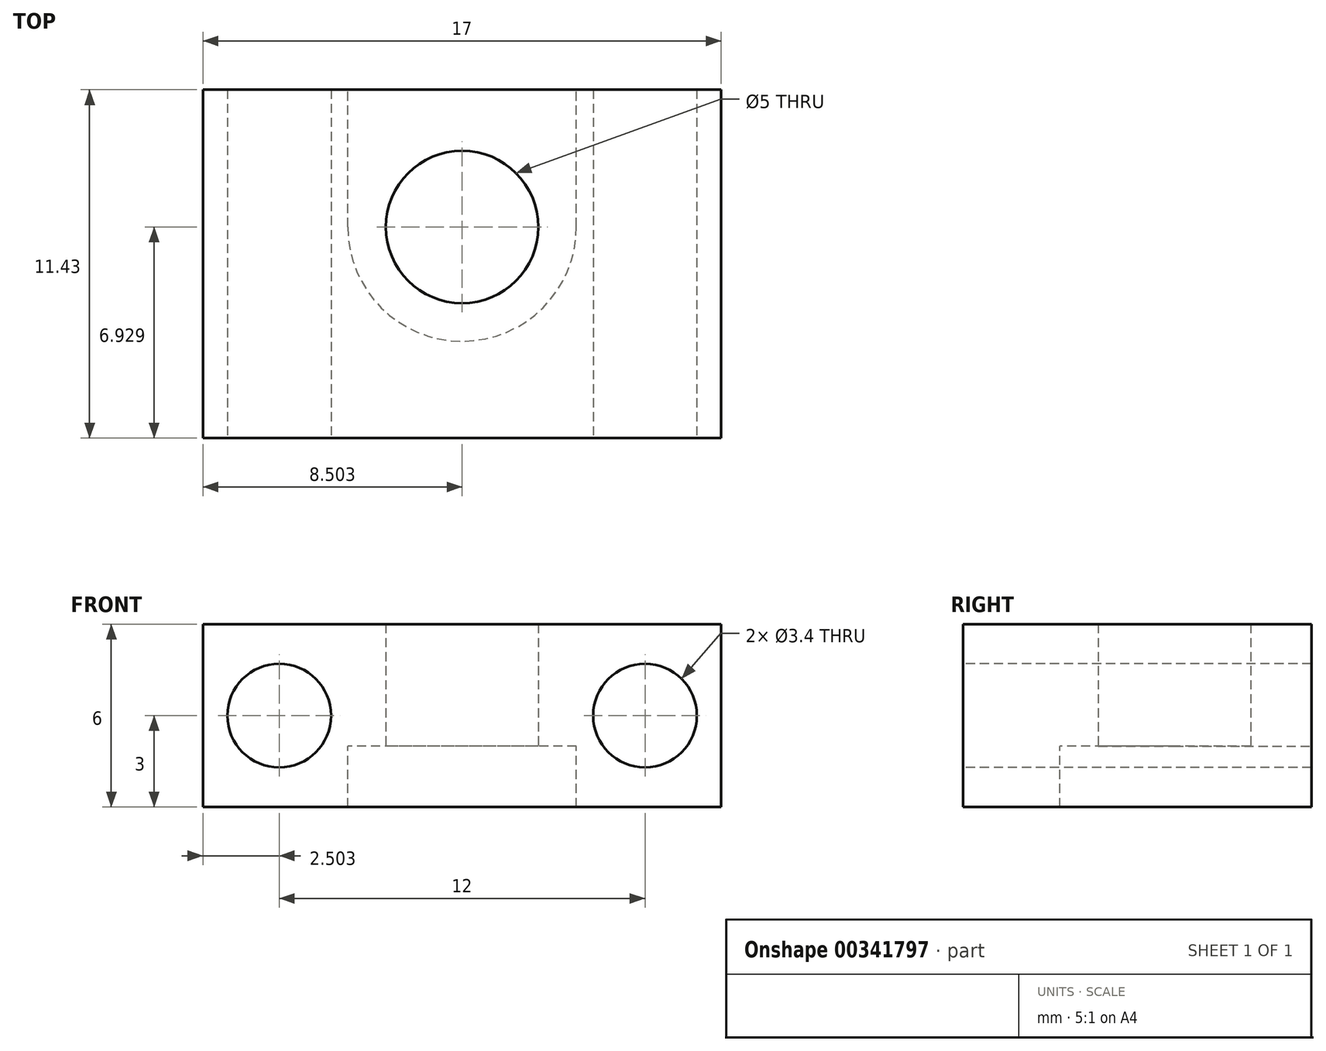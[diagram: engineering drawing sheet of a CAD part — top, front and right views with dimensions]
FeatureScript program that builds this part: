
annotation { "Feature Type Name" : "Feature", "Feature Type Description" : "" }
export const myFeature = defineFeature(function(context is Context, id is Id, definition is map)
    precondition{}
    {
        {
            var Q0;
            Q0=qCreatedBy(makeId("Top.planeOp"),FACE);
            var sketch = newSketch(context, id + "F0", { "sketchPlane" : qUnion([Q0])});
            skLineSegment(sketch, "E0.bottom", {"start": v(-26.33, 17.35) * mm, "end": v(-43.33, 17.35) * mm});
            skLineSegment(sketch, "E0.top", {"start": v(-26.33, 28.78) * mm, "end": v(-43.33, 28.78) * mm});
            skLineSegment(sketch, "E0.left", {"start": v(-26.33, 17.35) * mm, "end": v(-26.33, 28.78) * mm});
            skLineSegment(sketch, "E0.right", {"start": v(-43.33, 17.35) * mm, "end": v(-43.33, 28.78) * mm});
            skLineSegment(sketch, "E1", {"start": v(-34.83, 28.78) * mm, "end": v(-34.83, 17.35) * mm, "construction": true});
            skCircle(sketch, "E2", {"center": v(-34.83, 24.28) * mm, "radius": 2.5 * mm});
            skSolve(sketch);
        }
        {
            var Q0;
            Q0=makeQuery(id+"F0.imprint","IMPRINT",FACE,{"disambiguationData":[TD([[makeQuery(id+"F0.imprint","IMPRINT",EDGE,{"derivedFrom":sQuery(id+"F0.wireOp",EDGE,"E0.bottom")}),-1.0]])]});
            extrude(context, id + "F1", {"entities" : qUnion([Q0]), "depth" : 4 * mm});
        }
        {
            var Q0;
            Q0=makeQuery(id+"F1.opExtrude","CAP_FACE",FACE,{"disambiguationData":[OSD([sQuery(id+"F0.wireOp",EDGE,"E0.bottom"),sQuery(id+"F0.wireOp",EDGE,"E0.top"),sQuery(id+"F0.wireOp",EDGE,"E0.left"),sQuery(id+"F0.wireOp",EDGE,"E0.right"),sQuery(id+"F0.wireOp",EDGE,"E2")])],"isStart":true});
            var sketch = newSketch(context, id + "F2", { "sketchPlane" : qUnion([Q0])});
            skCircle(sketch, "E3.0", {"center": v(-34.83, -24.28) * mm, "radius": 2.5 * mm});
            skArc(sketch, "E4", {"start": v(-31.08, -24.28) * mm, "mid": v(-34.83, -20.53) * mm, "end": v(-38.58, -24.28) * mm});
            skLineSegment(sketch, "E5", {"start": v(-34.83, -28.78) * mm, "end": v(-34.83, -17.35) * mm, "construction": true});
            skLineSegment(sketch, "E6", {"start": v(-34.83, -24.28) * mm, "end": v(-31.08, -24.28) * mm, "construction": true});
            skLineSegment(sketch, "E7", {"start": v(-34.83, -24.28) * mm, "end": v(-38.58, -24.28) * mm, "construction": true});
            skLineSegment(sketch, "E8", {"start": v(-31.08, -24.28) * mm, "end": v(-31.08, -28.78) * mm});
            skLineSegment(sketch, "E9", {"start": v(-38.58, -24.28) * mm, "end": v(-38.58, -28.78) * mm});
            skSolve(sketch);
        }
        {
            var Q0;
            Q0=makeQuery(id+"F2.imprint","IMPRINT",FACE,{"disambiguationData":[TD([[makeQuery(id+"F2.imprint","IMPRINT",EDGE,{"derivedFrom":sQuery(id+"F2.wireOp",EDGE,"E4")}),-1.0]])]});
            extrude(context, id + "F3", {"entities" : qUnion([Q0]), "operationType" : NewBodyOperationType.ADD, "depth" : 2 * mm});
        }
        {
            var Q0;
            {var subQ0=sQuery(id+"F0.wireOp",EDGE,"E0.bottom");Q0=makeQuery(id+"F3.boolean.opBoolean","MERGE",FACE,{"derivedFrom":[makeQuery(id+"F1.opExtrude","SWEPT_FACE",FACE,{"disambiguationData":[OSD([subQ0])]}),makeQuery(id+"F3.opExtrude","SWEPT_FACE",FACE,{"disambiguationData":[OSD([subQ0])]})]});}
            var sketch = newSketch(context, id + "F4", { "sketchPlane" : qUnion([Q0])});
            skLineSegment(sketch, "E10", {"start": v(-34.83, -2) * mm, "end": v(-34.83, 4) * mm, "construction": true});
            skLineSegment(sketch, "E11", {"start": v(-26.33, 1) * mm, "end": v(-43.33, 1) * mm, "construction": true});
            skCircle(sketch, "E12", {"center": v(-28.83, 1) * mm, "radius": 1.7 * mm});
            skCircle(sketch, "E13", {"center": v(-40.83, 1) * mm, "radius": 1.7 * mm});
            skSolve(sketch);
        }
        {
            var Q0;
            Q0=makeQuery(id+"F4.imprint","IMPRINT",FACE,{"disambiguationData":[TD([[makeQuery(id+"F4.imprint","IMPRINT",EDGE,{"derivedFrom":sQuery(id+"F4.wireOp",EDGE,"E12")}),1.0]])]});
            var Q1;
            Q1=makeQuery(id+"F4.imprint","IMPRINT",FACE,{"disambiguationData":[TD([[makeQuery(id+"F4.imprint","IMPRINT",EDGE,{"derivedFrom":sQuery(id+"F4.wireOp",EDGE,"E13")}),1.0]])]});
            extrude(context, id + "F5", {"entities" : qUnion([Q0, Q1]), "operationType" : NewBodyOperationType.REMOVE, "endBound" : BoundingType.THROUGH_ALL, "oppositeDirection" : true, "depth" : 5.1 * mm});
        }
    });
